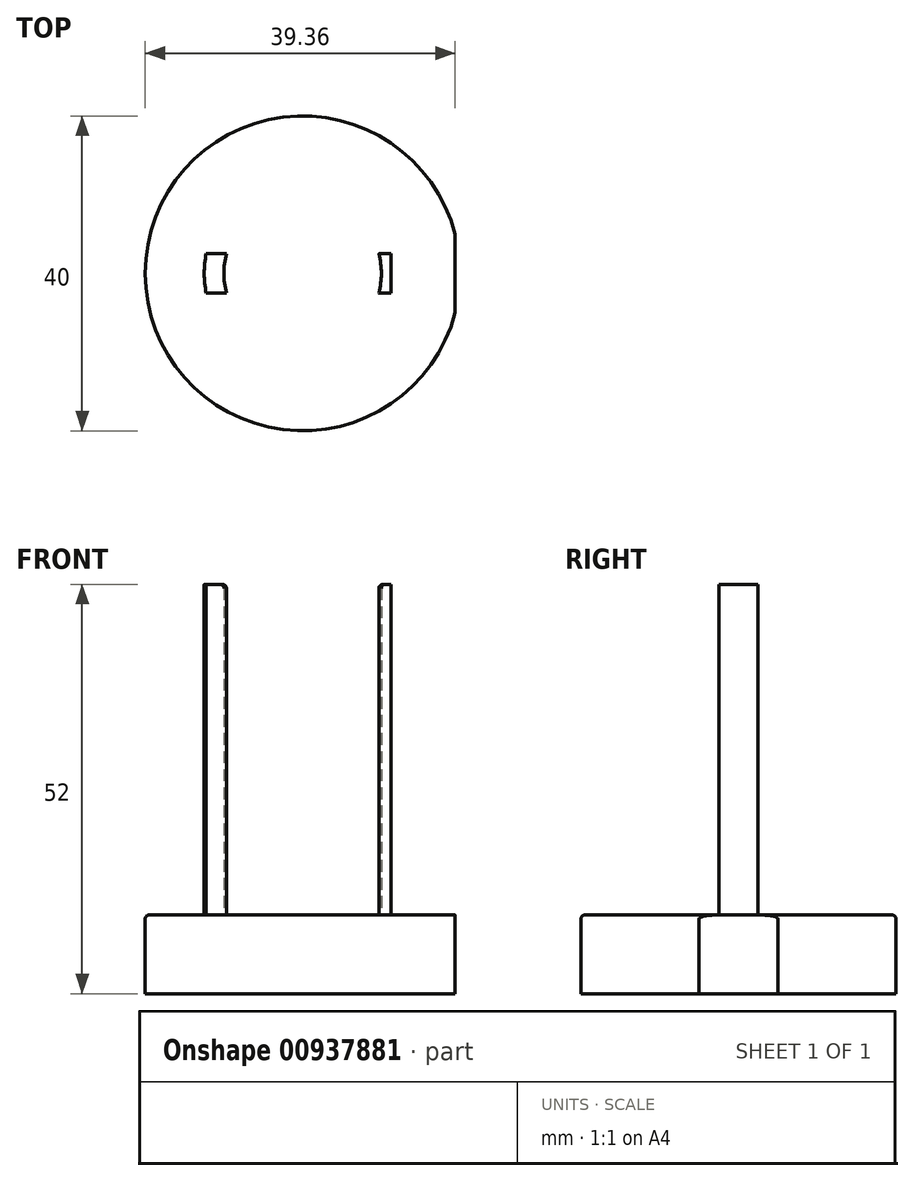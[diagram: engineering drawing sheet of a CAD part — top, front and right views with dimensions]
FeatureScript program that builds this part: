
annotation { "Feature Type Name" : "Feature", "Feature Type Description" : "" }
export const myFeature = defineFeature(function(context is Context, id is Id, definition is map)
    precondition{}
    {
        {
            var Q0;
            Q0=qCreatedBy(makeId("Top.planeOp"),FACE);
            var sketch = newSketch(context, id + "F0", { "sketchPlane" : qUnion([Q0])});
            skCircle(sketch, "E0", {"center": v(0, 0) * mm, "radius": 20 * mm});
            skLineSegment(sketch, "E1.bottom", {"start": v(19.36, -5) * mm, "end": v(-19.36, -5) * mm});
            skLineSegment(sketch, "E1.top", {"start": v(19.36, 5) * mm, "end": v(-19.36, 5) * mm});
            skLineSegment(sketch, "E1.left", {"start": v(19.36, -5) * mm, "end": v(19.36, 5) * mm});
            skLineSegment(sketch, "E1.right", {"start": v(-19.36, -5) * mm, "end": v(-19.36, 5) * mm});
            skSolve(sketch);
        }
        {
            var Q0;
            {var subQ0=sQuery(id+"F0.wireOp",EDGE,"E1.top");Q0=makeQuery(id+"F0.imprint","IMPRINT",FACE,{"disambiguationData":[TD([[makeQuery(id+"F0.imprint","IMPRINT",EDGE,{"derivedFrom":subQ0}),-1.0]])]});}
            var Q1;
            {var subQ0=sQuery(id+"F0.wireOp",EDGE,"E1.right");Q1=makeQuery(id+"F0.imprint","IMPRINT",FACE,{"disambiguationData":[TD([[makeQuery(id+"F0.imprint","IMPRINT",EDGE,{"derivedFrom":subQ0}),1.0]])]});}
            var Q2;
            {var subQ0=sQuery(id+"F0.wireOp",EDGE,"E1.bottom");Q2=makeQuery(id+"F0.imprint","IMPRINT",FACE,{"disambiguationData":[TD([[makeQuery(id+"F0.imprint","IMPRINT",EDGE,{"derivedFrom":subQ0}),1.0]])]});}
            var Q3;
            Q3=makeQuery(id+"F0.imprint","IMPRINT",FACE,{"disambiguationData":[TD([[makeQuery(id+"F0.imprint","IMPRINT",EDGE,{"derivedFrom":sQuery(id+"F0.wireOp",EDGE,"E1.bottom")}),-1.0]])]});
            extrude(context, id + "F1", {"entities" : qUnion([Q0, Q1, Q2, Q3]), "oppositeDirection" : true, "depth" : 10 * mm, "offsetDistance" : 25.4 * mm});
        }
        {
            var Q0;
            Q0=makeQuery(id+"F1.opExtrude","CAP_FACE",FACE,{"disambiguationData":[OSD([sQuery(id+"F0.wireOp",EDGE,"E0")])],"isStart":true});
            var sketch = newSketch(context, id + "F2", { "sketchPlane" : qUnion([Q0])});
            skCircle(sketch, "E2", {"center": v(0, 0) * mm, "radius": 12.5 * mm});
            skCircle(sketch, "E3", {"center": v(0, 0) * mm, "radius": 10 * mm});
            skLineSegment(sketch, "E4.bottom", {"start": v(12.25, 2.5) * mm, "end": v(-12.25, 2.5) * mm});
            skLineSegment(sketch, "E4.top", {"start": v(12.25, -2.5) * mm, "end": v(-12.25, -2.5) * mm});
            skLineSegment(sketch, "E4.left", {"start": v(12.25, 2.5) * mm, "end": v(12.25, -2.5) * mm});
            skLineSegment(sketch, "E4.right", {"start": v(-12.25, 2.5) * mm, "end": v(-12.25, -2.5) * mm});
            skLineSegment(sketch, "E5", {"start": v(11.25, 2.5) * mm, "end": v(11.25, -2.5) * mm});
            skSolve(sketch);
        }
        {
            var Q0;
            {var subQ0=sQuery(id+"F2.wireOp",EDGE,"E4.bottom");var subQ4=sQuery(id+"F2.wireOp",EDGE,"E3");var subQ6=makeQuery(id+"F2.imprint","INTERSECT",VERTEX,{"disambiguationData":[OD(0.0)],"derivedFrom":[subQ4,subQ0]});Q0=makeQuery(id+"F2.imprint","IMPRINT",FACE,{"disambiguationData":[TD([[makeQuery(id+"F2.imprint","IMPRINT",EDGE,{"disambiguationData":[TD([[subQ6,1.0]])],"derivedFrom":subQ4}),-1.0]])]});}
            var Q1;
            {var subQ5=sQuery(id+"F2.wireOp",EDGE,"E5");Q1=makeQuery(id+"F2.imprint","IMPRINT",FACE,{"disambiguationData":[TD([[makeQuery(id+"F2.imprint","IMPRINT",EDGE,{"derivedFrom":subQ5}),-1.0]])]});}
            var Q2;
            {var subQ0=sQuery(id+"F2.wireOp",EDGE,"E4.top");var subQ2=sQuery(id+"F2.wireOp",EDGE,"E3");var subQ7=makeQuery(id+"F2.imprint","INTERSECT",VERTEX,{"disambiguationData":[OD(0.0)],"derivedFrom":[subQ2,subQ0]});Q2=makeQuery(id+"F2.imprint","IMPRINT",FACE,{"disambiguationData":[TD([[makeQuery(id+"F2.imprint","IMPRINT",EDGE,{"disambiguationData":[TD([[subQ7,-1.0]])],"derivedFrom":subQ2}),-1.0]])]});}
            var Q3;
            {var subQ5=sQuery(id+"F2.wireOp",EDGE,"E4.right");Q3=makeQuery(id+"F2.imprint","IMPRINT",FACE,{"disambiguationData":[TD([[makeQuery(id+"F2.imprint","IMPRINT",EDGE,{"derivedFrom":subQ5}),1.0]])]});}
            var Q4;
            {var subQ0=sQuery(id+"F2.wireOp",EDGE,"E4.right");Q4=makeQuery(id+"F2.imprint","IMPRINT",FACE,{"disambiguationData":[TD([[makeQuery(id+"F2.imprint","IMPRINT",EDGE,{"derivedFrom":subQ0}),-1.0]])]});}
            extrude(context, id + "F3", {"entities" : qUnion([Q0, Q1, Q2, Q3, Q4]), "operationType" : NewBodyOperationType.ADD, "depth" : 42 * mm, "offsetDistance" : 25.4 * mm});
        }
        {
            var Q0;
            Q0=makeQuery(id+"F3.opExtrude","CAP_EDGE",EDGE,{"disambiguationData":[OSD([sQuery(id+"F2.wireOp",EDGE,"E3")])],"isStart":false});
            var Q1;
            Q1=makeQuery(id+"F3.opExtrude","CAP_EDGE",EDGE,{"disambiguationData":[OSD([sQuery(id+"F2.wireOp",EDGE,"E2")])],"isStart":true});
            var Q2;
            Q2=makeQuery(id+"F1.opExtrude","CAP_EDGE",EDGE,{"disambiguationData":[OSD([sQuery(id+"F0.wireOp",EDGE,"E0")])],"isStart":true});
            fillet(context, id + "F4", {"entities" : qUnion([Q0, Q1, Q2]), "radius" : 0.5 * mm, "tangentPropagation" : true, "allowEdgeOverflow" : false});
        }
    });
